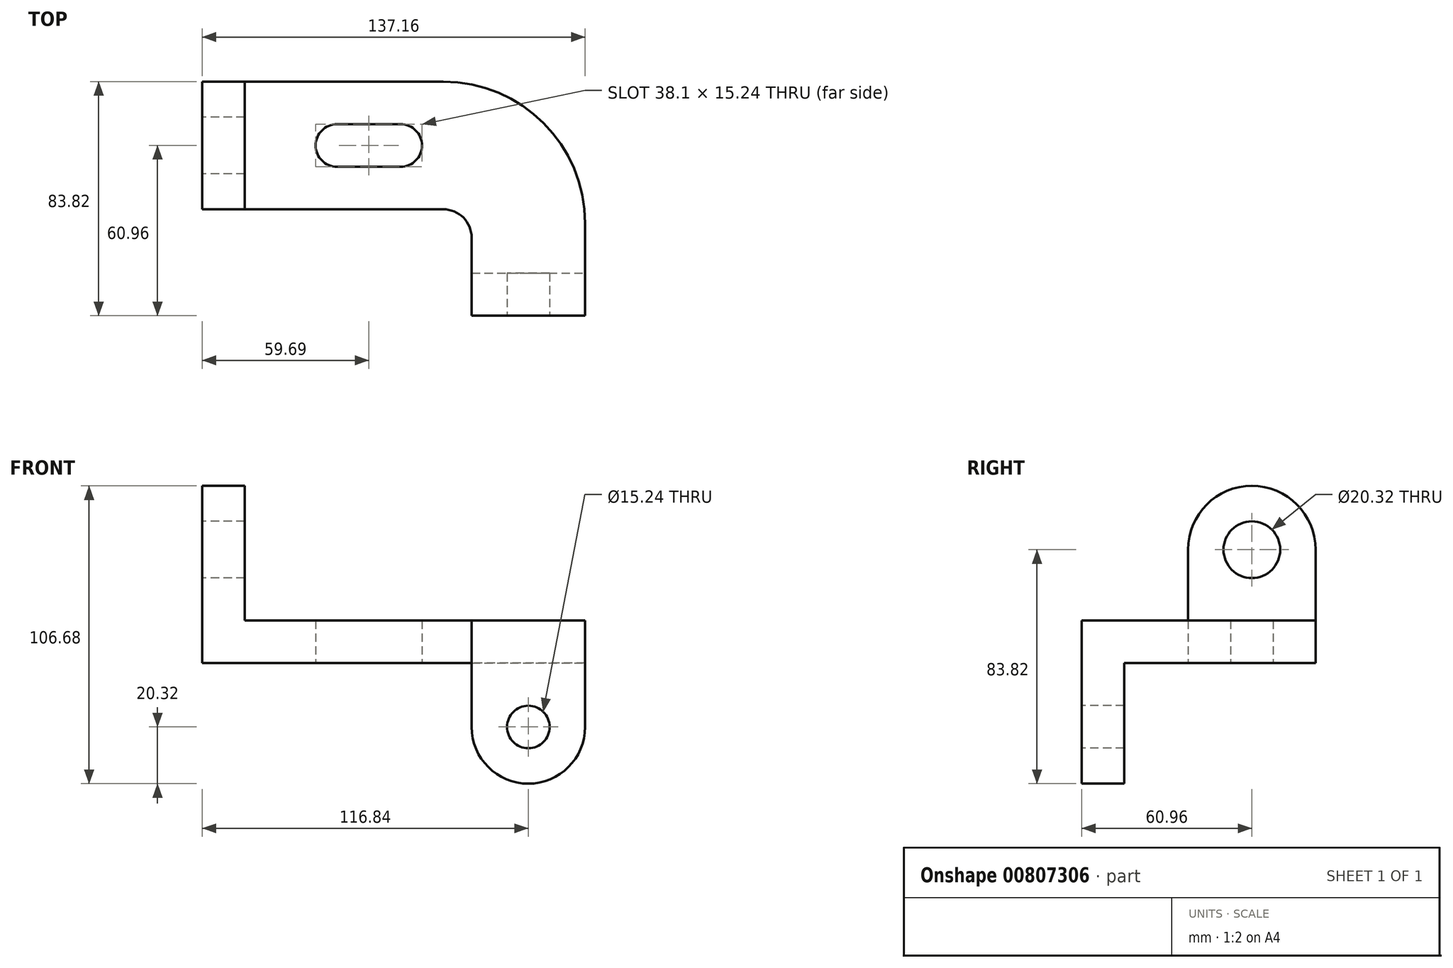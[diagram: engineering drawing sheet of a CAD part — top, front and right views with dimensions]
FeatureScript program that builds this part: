
annotation { "Feature Type Name" : "Feature", "Feature Type Description" : "" }
export const myFeature = defineFeature(function(context is Context, id is Id, definition is map)
    precondition{}
    {
        {
            var Q0;
            Q0=qCreatedBy(makeId("Top.planeOp"),FACE);
            var sketch = newSketch(context, id + "F0", { "sketchPlane" : qUnion([Q0])});
            skLineSegment(sketch, "E0", {"start": v(0, 0) * mm, "end": v(0, 45.72) * mm});
            skLineSegment(sketch, "E1", {"start": v(0, 45.72) * mm, "end": v(86.36, 45.72) * mm});
            skLineSegment(sketch, "E2", {"start": v(137.16, -5.08) * mm, "end": v(137.16, -38.1) * mm});
            skLineSegment(sketch, "E3", {"start": v(137.16, -38.1) * mm, "end": v(96.52, -38.1) * mm});
            skLineSegment(sketch, "E4", {"start": v(96.52, -38.1) * mm, "end": v(96.52, -10.16) * mm});
            skLineSegment(sketch, "E5", {"start": v(86.36, 0) * mm, "end": v(0, 0) * mm});
            skPoint(sketch, "E6", {"position": v(116.84, -38.1) * mm});
            skPoint(sketch, "E7", {"position": v(0, 22.86) * mm});
            skLineSegment(sketch, "E8", {"start": v(15.24, 45.72) * mm, "end": v(15.24, 0) * mm});
            skLineSegment(sketch, "E9", {"start": v(96.52, -22.86) * mm, "end": v(137.16, -22.86) * mm});
            skLineSegment(sketch, "E10", {"start": v(48.26, 30.48) * mm, "end": v(71.12, 30.48) * mm});
            skLineSegment(sketch, "E11", {"start": v(48.26, 15.24) * mm, "end": v(71.12, 15.24) * mm});
            skArc(sketch, "E12", {"start": v(48.26, 30.48) * mm, "mid": v(40.64, 22.86) * mm, "end": v(48.26, 15.24) * mm});
            skArc(sketch, "E13", {"start": v(48.26, 15.24) * mm, "mid": v(55.88, 22.86) * mm, "end": v(48.26, 30.48) * mm, "construction": true});
            skLineSegment(sketch, "E14", {"start": v(71.12, 15.24) * mm, "end": v(71.12, 15.24) * mm});
            skArc(sketch, "E15", {"start": v(71.12, 30.48) * mm, "mid": v(63.5, 22.86) * mm, "end": v(71.12, 15.24) * mm, "construction": true});
            skArc(sketch, "E16", {"start": v(71.12, 15.24) * mm, "mid": v(78.74, 22.86) * mm, "end": v(71.12, 30.48) * mm});
            skPoint(sketch, "E17.visualSharp", {"position": v(96.52, 0) * mm});
            skArc(sketch, "E17.filletArc", {"start": v(96.52, -10.16) * mm, "mid": v(93.54, -2.98) * mm, "end": v(86.36, 0) * mm});
            skPoint(sketch, "E18.visualSharp", {"position": v(137.16, 45.72) * mm});
            skArc(sketch, "E18.filletArc", {"start": v(137.16, -5.08) * mm, "mid": v(122.28, 30.84) * mm, "end": v(86.36, 45.72) * mm});
            skSolve(sketch);
        }
        {
            var Q0;
            {var subQ1=sQuery(id+"F0.wireOp",EDGE,"E8");Q0=makeQuery(id+"F0.imprint","IMPRINT",FACE,{"disambiguationData":[TD([[makeQuery(id+"F0.imprint","IMPRINT",EDGE,{"derivedFrom":subQ1}),1.0]])]});}
            var Q1;
            {var subQ0=sQuery(id+"F0.wireOp",EDGE,"E0");Q1=makeQuery(id+"F0.imprint","IMPRINT",FACE,{"disambiguationData":[TD([[makeQuery(id+"F0.imprint","IMPRINT",EDGE,{"derivedFrom":subQ0}),-1.0]])]});}
            var Q2;
            {var subQ0=sQuery(id+"F0.wireOp",EDGE,"E3");Q2=makeQuery(id+"F0.imprint","IMPRINT",FACE,{"disambiguationData":[TD([[makeQuery(id+"F0.imprint","IMPRINT",EDGE,{"derivedFrom":subQ0}),-1.0]])]});}
            extrude(context, id + "F1", {"entities" : qUnion([Q0, Q1, Q2]), "depth" : 15.24 * mm, "offsetDistance" : 25.4 * mm});
        }
        {
            var Q0;
            {var subQ0=sQuery(id+"F0.wireOp",EDGE,"E0");Q0=makeQuery(id+"F0.imprint","IMPRINT",FACE,{"disambiguationData":[TD([[makeQuery(id+"F0.imprint","IMPRINT",EDGE,{"derivedFrom":subQ0}),-1.0]])]});}
            extrude(context, id + "F2", {"entities" : qUnion([Q0]), "operationType" : NewBodyOperationType.ADD, "depth" : 63.5 * mm, "offsetDistance" : 25.4 * mm});
        }
        {
            var Q0;
            {var subQ0=sQuery(id+"F0.wireOp",EDGE,"E3");Q0=makeQuery(id+"F0.imprint","IMPRINT",FACE,{"disambiguationData":[TD([[makeQuery(id+"F0.imprint","IMPRINT",EDGE,{"derivedFrom":subQ0}),-1.0]])]});}
            extrude(context, id + "F3", {"entities" : qUnion([Q0]), "operationType" : NewBodyOperationType.ADD, "oppositeDirection" : true, "depth" : 43.18 * mm, "offsetDistance" : 25.4 * mm});
        }
        {
            var Q0;
            {var subQ0=sQuery(id+"F0.wireOp",EDGE,"E0");Q0=makeQuery(id+"F2.boolean.opBoolean","MERGE",FACE,{"derivedFrom":[makeQuery(id+"F1.opExtrude","SWEPT_FACE",FACE,{"disambiguationData":[OSD([subQ0])]}),makeQuery(id+"F2.opExtrude","SWEPT_FACE",FACE,{"disambiguationData":[OSD([subQ0])]})]});}
            var sketch = newSketch(context, id + "F4", { "sketchPlane" : qUnion([Q0])});
            skLineSegment(sketch, "E19.0.0", {"start": v(-45.72, 0) * mm, "end": v(0, 0) * mm});
            skLineSegment(sketch, "E19.0.1", {"start": v(0, 0) * mm, "end": v(0, 63.5) * mm});
            skLineSegment(sketch, "E19.0.2", {"start": v(0, 63.5) * mm, "end": v(-45.72, 63.5) * mm});
            skLineSegment(sketch, "E19.0.3", {"start": v(-45.72, 63.5) * mm, "end": v(-45.72, 0) * mm});
            skPoint(sketch, "E20", {"position": v(-22.86, 63.5) * mm});
            skPoint(sketch, "E21", {"position": v(-22.86, 0) * mm});
            skLineSegment(sketch, "E22", {"start": v(-22.86, 63.5) * mm, "end": v(-22.86, 0) * mm, "construction": true});
            skCircle(sketch, "E23", {"center": v(-22.86, 40.64) * mm, "radius": 10.16 * mm});
            skArc(sketch, "E24", {"start": v(-45.72, 40.64) * mm, "mid": v(-22.86, 17.78) * mm, "end": v(0, 40.64) * mm, "construction": true});
            skArc(sketch, "E25", {"start": v(0, 40.64) * mm, "mid": v(-22.86, 63.5) * mm, "end": v(-45.72, 40.64) * mm});
            skSolve(sketch);
        }
        {
            var Q0;
            {var subQ0=sQuery(id+"F4.wireOp",EDGE,"E19.0.2");var subQ1=sQuery(id+"F4.wireOp",EDGE,"E19.0.1");var subQ2=makeQuery(id+"F4.imprint","INTERSECT",VERTEX,{"derivedFrom":[subQ1,subQ0]});Q0=makeQuery(id+"F4.imprint","IMPRINT",FACE,{"disambiguationData":[TD([[makeQuery(id+"F4.imprint","IMPRINT",EDGE,{"disambiguationData":[TD([[subQ2,-1.0]])],"derivedFrom":subQ1}),-1.0]])]});}
            var Q1;
            {var subQ0=sQuery(id+"F4.wireOp",EDGE,"E19.0.3");var subQ1=sQuery(id+"F4.wireOp",EDGE,"E19.0.2");var subQ2=makeQuery(id+"F4.imprint","INTERSECT",VERTEX,{"derivedFrom":[subQ1,subQ0]});Q1=makeQuery(id+"F4.imprint","IMPRINT",FACE,{"disambiguationData":[TD([[makeQuery(id+"F4.imprint","IMPRINT",EDGE,{"disambiguationData":[TD([[subQ2,1.0]])],"derivedFrom":subQ1}),1.0]])]});}
            var Q2;
            Q2=makeQuery(id+"F4.imprint","IMPRINT",FACE,{"disambiguationData":[TD([[makeQuery(id+"F4.imprint","IMPRINT",EDGE,{"derivedFrom":sQuery(id+"F4.wireOp",EDGE,"E23")}),1.0]])]});
            var Q3;
            Q3=makeQuery(id+"F2.opExtrude","SWEPT_FACE",FACE,{"disambiguationData":[OSD([sQuery(id+"F0.wireOp",EDGE,"E8")])]});
            extrude(context, id + "F5", {"entities" : qUnion([Q0, Q1, Q2]), "operationType" : NewBodyOperationType.REMOVE, "endBound" : BoundingType.UP_TO_SURFACE, "oppositeDirection" : true, "depth" : 25.4 * mm, "endBoundEntityFace" : qUnion([Q3]), "offsetDistance" : 25.4 * mm});
        }
        {
            var Q0;
            {var subQ0=sQuery(id+"F0.wireOp",EDGE,"E3");Q0=makeQuery(id+"F3.boolean.opBoolean","MERGE",FACE,{"derivedFrom":[makeQuery(id+"F1.opExtrude","SWEPT_FACE",FACE,{"disambiguationData":[OSD([subQ0])]}),makeQuery(id+"F3.opExtrude","SWEPT_FACE",FACE,{"disambiguationData":[OSD([subQ0])]})]});}
            var sketch = newSketch(context, id + "F6", { "sketchPlane" : qUnion([Q0])});
            skLineSegment(sketch, "E26.0.0", {"start": v(96.52, 15.24) * mm, "end": v(96.52, -43.18) * mm});
            skLineSegment(sketch, "E26.0.1", {"start": v(96.52, -43.18) * mm, "end": v(137.16, -43.18) * mm});
            skLineSegment(sketch, "E26.0.2", {"start": v(137.16, -43.18) * mm, "end": v(137.16, 15.24) * mm});
            skLineSegment(sketch, "E26.0.3", {"start": v(137.16, 15.24) * mm, "end": v(96.52, 15.24) * mm});
            skPoint(sketch, "E27", {"position": v(116.84, 15.24) * mm});
            skPoint(sketch, "E28", {"position": v(116.84, -43.18) * mm});
            skLineSegment(sketch, "E29", {"start": v(116.84, 15.24) * mm, "end": v(116.84, -43.18) * mm, "construction": true});
            skCircle(sketch, "E30", {"center": v(116.84, -22.86) * mm, "radius": 7.62 * mm});
            skArc(sketch, "E31", {"start": v(96.52, -22.86) * mm, "mid": v(116.84, -43.18) * mm, "end": v(137.16, -22.86) * mm});
            skArc(sketch, "E32", {"start": v(137.16, -22.86) * mm, "mid": v(116.84, -2.54) * mm, "end": v(96.52, -22.86) * mm, "construction": true});
            skSolve(sketch);
        }
        {
            var Q0;
            {var subQ0=sQuery(id+"F6.wireOp",EDGE,"E26.0.2");var subQ1=sQuery(id+"F6.wireOp",EDGE,"E26.0.1");var subQ2=makeQuery(id+"F6.imprint","INTERSECT",VERTEX,{"derivedFrom":[subQ1,subQ0]});Q0=makeQuery(id+"F6.imprint","IMPRINT",FACE,{"disambiguationData":[TD([[makeQuery(id+"F6.imprint","IMPRINT",EDGE,{"disambiguationData":[TD([[subQ2,-1.0]])],"derivedFrom":subQ1}),-1.0]])]});}
            var Q1;
            {var subQ0=sQuery(id+"F6.wireOp",EDGE,"E26.0.1");var subQ1=sQuery(id+"F6.wireOp",EDGE,"E26.0.0");var subQ2=makeQuery(id+"F6.imprint","INTERSECT",VERTEX,{"derivedFrom":[subQ1,subQ0]});Q1=makeQuery(id+"F6.imprint","IMPRINT",FACE,{"disambiguationData":[TD([[makeQuery(id+"F6.imprint","IMPRINT",EDGE,{"disambiguationData":[TD([[subQ2,1.0]])],"derivedFrom":subQ1}),1.0]])]});}
            var Q2;
            Q2=makeQuery(id+"F6.imprint","IMPRINT",FACE,{"disambiguationData":[TD([[makeQuery(id+"F6.imprint","IMPRINT",EDGE,{"derivedFrom":sQuery(id+"F6.wireOp",EDGE,"E30")}),1.0]])]});
            var Q3;
            Q3=makeQuery(id+"F3.opExtrude","SWEPT_FACE",FACE,{"disambiguationData":[OSD([sQuery(id+"F0.wireOp",EDGE,"E9")])]});
            extrude(context, id + "F7", {"entities" : qUnion([Q0, Q1, Q2]), "operationType" : NewBodyOperationType.REMOVE, "endBound" : BoundingType.UP_TO_SURFACE, "oppositeDirection" : true, "depth" : 25.4 * mm, "endBoundEntityFace" : qUnion([Q3]), "offsetDistance" : 25.4 * mm});
        }
    });
